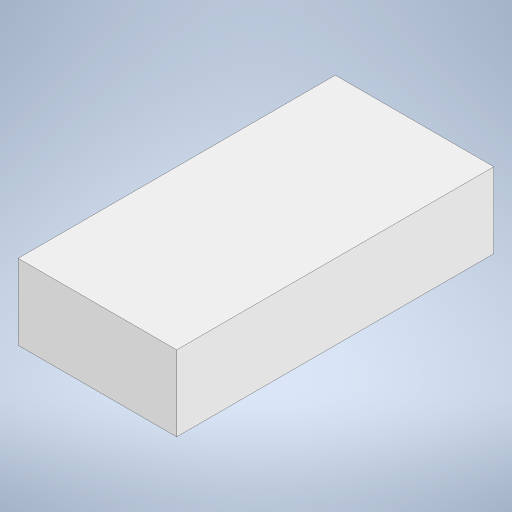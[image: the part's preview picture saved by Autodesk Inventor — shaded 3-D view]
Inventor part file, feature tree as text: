
AUTODESK INVENTOR PART (.ipt)
format: ipt  version: 2024 (Build 280153000, 153)  size: 185,856 bytes
history: native  units: in
note: dims shown in document units (in); Inventor stores cm internally (conversion verified against a paired STEP export)
features: extrude x1, sketch x1
ambient origin geometry x8: Origin, YZ Plane, XZ Plane, XY Plane, X Axis, Y Axis, Z Axis, Center Point
bodies: Solid1 (feature_tree)
feature tree (2):
  extrude  "Extrusion1"  Depth=14.25in
  sketch  "Sketch1"  dims[d0=60.0in d2=14.25in d3=30.0in d4=0.0in]
